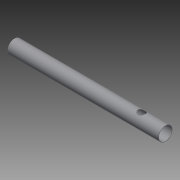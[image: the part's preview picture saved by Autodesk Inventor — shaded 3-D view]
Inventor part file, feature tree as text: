
AUTODESK INVENTOR PART (.ipt)
format: ipt  version: 2014 SP2 (Build 180246200, 246)  size: 82,944 bytes
history: native  units: mm
features: extrude x2, sketch x2
ambient origin geometry x8: Origin, YZ Plane, XZ Plane, XY Plane, X Axis, Y Axis, Z Axis, Center Point
bodies: Solid1 (feature_tree)
feature tree (4):
  extrude  "Extrusion1"  Depth=17.5mm
  extrude  "Extrusion2"  Depth=10.0mm
  sketch  "Sketch1"  dims[d0=18.5mm d1=17.5mm]
  sketch  "Sketch2"  dims[d2=200.0mm d3=0.0mm d4=10.0mm d5=200.0mm d6=0.0mm]
